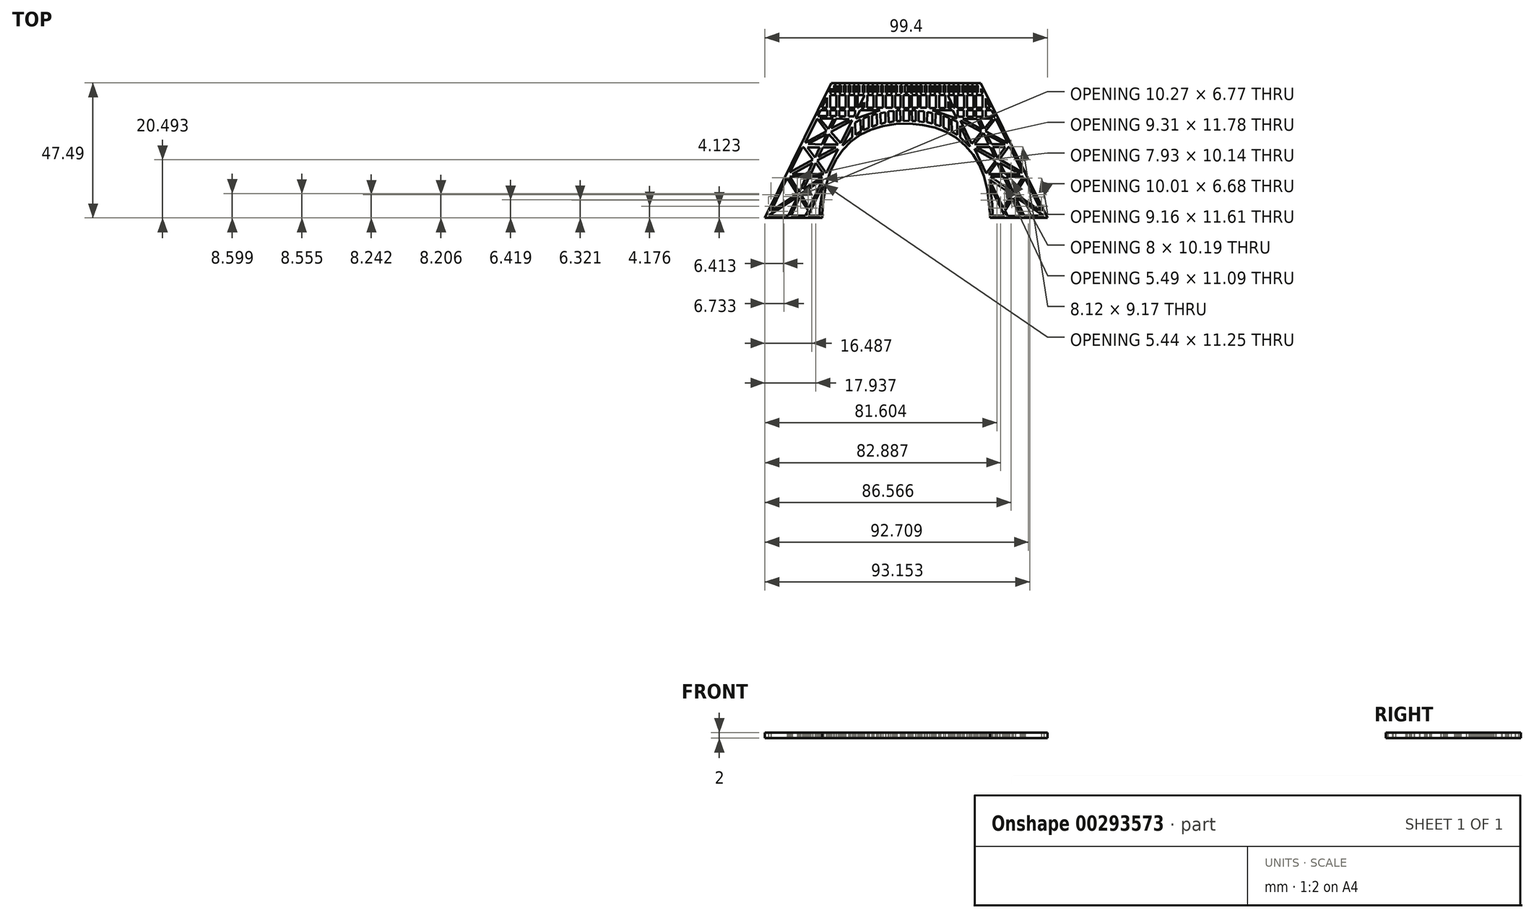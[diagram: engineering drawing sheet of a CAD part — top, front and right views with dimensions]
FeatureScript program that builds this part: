
annotation { "Feature Type Name" : "Feature", "Feature Type Description" : "" }
export const myFeature = defineFeature(function(context is Context, id is Id, definition is map)
    precondition{}
    {
        {
            var Q0;
            Q0=qCreatedBy(makeId("Top.planeOp"),FACE);
            var sketch = newSketch(context, id + "F0", { "sketchPlane" : qUnion([Q0])});
            skLineSegment(sketch, "E0", {"start": v(-25.5, 30.2) * mm, "end": v(27, 30.2) * mm});
            skLineSegment(sketch, "E1", {"start": v(27, 30.2) * mm, "end": v(50.51, -17.28) * mm});
            skLineSegment(sketch, "E2", {"start": v(50.51, -17.28) * mm, "end": v(30.37, -17.28) * mm});
            skFitSpline(sketch, "E3", {"points": [v(30.37, -17.28) * mm, v(28.52, -3.68) * mm, v(23.88, 5.66) * mm, v(16.6, 12.1) * mm, v(7.11, 15.39) * mm, v(-5.07, 15.52) * mm, v(-15.11, 12.1) * mm, v(-21.96, 6.08) * mm, v(-27.14, -4.88) * mm, v(-28.74, -16.53) * mm, v(-28.73, -17.28) * mm], "startDerivative": vector(-8.93, 118.35) * mm, "endDerivative": vector(1.13, -17.93) * mm});
            skLineSegment(sketch, "E4", {"start": v(-28.73, -17.28) * mm, "end": v(-48.89, -17.28) * mm});
            skLineSegment(sketch, "E5", {"start": v(-48.89, -17.28) * mm, "end": v(-25.5, 30.2) * mm});
            skFitSpline(sketch, "E6", {"points": [v(-28.23, -5.24) * mm, v(-29.56, -14.09) * mm, v(-29.62, -16.49) * mm], "startDerivative": vector(-2.61, -15.55) * mm, "endDerivative": vector(0.12, -5.94) * mm});
            skLineSegment(sketch, "E7", {"start": v(-29.62, -16.49) * mm, "end": v(-33.67, -16.49) * mm});
            skLineSegment(sketch, "E8", {"start": v(-33.67, -16.49) * mm, "end": v(-28.23, -5.24) * mm});
            skLineSegment(sketch, "E9", {"start": v(-33.67, -14.65) * mm, "end": v(-34.75, -16.49) * mm});
            skLineSegment(sketch, "E10", {"start": v(-34.75, -16.49) * mm, "end": v(-39.64, -16.49) * mm});
            skLineSegment(sketch, "E11", {"start": v(-39.64, -16.49) * mm, "end": v(-36.7, -10.13) * mm});
            skLineSegment(sketch, "E12", {"start": v(-36.7, -10.13) * mm, "end": v(-33.67, -14.65) * mm});
            skLineSegment(sketch, "E13", {"start": v(-47.61, -16.49) * mm, "end": v(-40.68, -16.49) * mm});
            skLineSegment(sketch, "E14", {"start": v(-40.68, -16.49) * mm, "end": v(-37.34, -9.72) * mm});
            skLineSegment(sketch, "E15", {"start": v(-37.34, -9.72) * mm, "end": v(-47.61, -16.49) * mm});
            skLineSegment(sketch, "E16", {"start": v(-41.01, -3.15) * mm, "end": v(-46.81, -14.93) * mm});
            skLineSegment(sketch, "E17", {"start": v(-46.81, -14.93) * mm, "end": v(-37.5, -8.8) * mm});
            skLineSegment(sketch, "E18", {"start": v(-37.5, -8.8) * mm, "end": v(-41.01, -3.15) * mm});
            skLineSegment(sketch, "E19", {"start": v(-33.43, -13.8) * mm, "end": v(-28.44, -3.66) * mm});
            skLineSegment(sketch, "E20", {"start": v(-28.44, -3.66) * mm, "end": v(-36.37, -8.88) * mm});
            skLineSegment(sketch, "E21", {"start": v(-36.37, -8.88) * mm, "end": v(-33.43, -13.8) * mm});
            skLineSegment(sketch, "E22", {"start": v(-40.2, -2.8) * mm, "end": v(-36.84, -8.21) * mm});
            skLineSegment(sketch, "E23", {"start": v(-36.84, -8.21) * mm, "end": v(-34.34, -2.8) * mm});
            skLineSegment(sketch, "E24", {"start": v(-34.34, -2.8) * mm, "end": v(-40.2, -2.8) * mm});
            skLineSegment(sketch, "E25", {"start": v(-35.31, -7.16) * mm, "end": v(-33.3, -2.8) * mm});
            skLineSegment(sketch, "E26", {"start": v(-33.3, -2.8) * mm, "end": v(-28.75, -2.8) * mm});
            skLineSegment(sketch, "E27", {"start": v(-28.75, -2.8) * mm, "end": v(-35.31, -7.16) * mm});
            skLineSegment(sketch, "E28", {"start": v(-39.29, -1.84) * mm, "end": v(-33.91, -1.84) * mm});
            skLineSegment(sketch, "E29", {"start": v(-33.91, -1.84) * mm, "end": v(-32.1, 2.1) * mm});
            skLineSegment(sketch, "E30", {"start": v(-32.1, 2.1) * mm, "end": v(-39.29, -1.84) * mm});
            skLineSegment(sketch, "E31", {"start": v(-31.01, 2.09) * mm, "end": v(-32.82, -1.84) * mm});
            skLineSegment(sketch, "E32", {"start": v(-32.82, -1.84) * mm, "end": v(-28.23, -1.84) * mm});
            skLineSegment(sketch, "E33", {"start": v(-28.23, -1.84) * mm, "end": v(-31.01, 2.09) * mm});
            skLineSegment(sketch, "E34", {"start": v(-30.53, 3) * mm, "end": v(-27.3, -1.46) * mm});
            skLineSegment(sketch, "E35", {"start": v(-27.3, -1.46) * mm, "end": v(-23.16, 6.95) * mm});
            skLineSegment(sketch, "E36", {"start": v(-23.16, 6.95) * mm, "end": v(-30.53, 3) * mm});
            skLineSegment(sketch, "E37", {"start": v(-40.2, -1.24) * mm, "end": v(-31.98, 3.22) * mm});
            skLineSegment(sketch, "E38", {"start": v(-31.98, 3.22) * mm, "end": v(-35.14, 7.6) * mm});
            skLineSegment(sketch, "E39", {"start": v(-35.14, 7.6) * mm, "end": v(-35.7, 7.6) * mm});
            skLineSegment(sketch, "E40", {"start": v(-35.7, 7.6) * mm, "end": v(-40.2, -1.24) * mm});
            skLineSegment(sketch, "E41", {"start": v(-33.97, 7.6) * mm, "end": v(-29.62, 7.6) * mm});
            skLineSegment(sketch, "E42", {"start": v(-29.62, 7.6) * mm, "end": v(-31.3, 3.94) * mm});
            skLineSegment(sketch, "E43", {"start": v(-31.3, 3.94) * mm, "end": v(-33.97, 7.6) * mm});
            skLineSegment(sketch, "E44", {"start": v(-28.53, 7.6) * mm, "end": v(-23.86, 7.6) * mm});
            skLineSegment(sketch, "E45", {"start": v(-23.86, 7.6) * mm, "end": v(-30.07, 4.3) * mm});
            skLineSegment(sketch, "E46", {"start": v(-30.07, 4.3) * mm, "end": v(-28.53, 7.6) * mm});
            skLineSegment(sketch, "E47", {"start": v(-29.62, 17.76) * mm, "end": v(-24.84, 17.76) * mm});
            skLineSegment(sketch, "E48", {"start": v(-24.84, 17.76) * mm, "end": v(-26.57, 14.02) * mm});
            skLineSegment(sketch, "E49", {"start": v(-26.57, 14.02) * mm, "end": v(-29.62, 17.76) * mm});
            skLineSegment(sketch, "E50", {"start": v(-23.93, 17.76) * mm, "end": v(-25.55, 14.27) * mm});
            skLineSegment(sketch, "E51", {"start": v(-25.55, 14.27) * mm, "end": v(-19.23, 17.4) * mm});
            skLineSegment(sketch, "E52", {"start": v(-19.23, 17.4) * mm, "end": v(-23.93, 17.76) * mm});
            skLineSegment(sketch, "E53", {"start": v(-30.53, 17.76) * mm, "end": v(-34.72, 9.24) * mm});
            skLineSegment(sketch, "E54", {"start": v(-34.72, 9.24) * mm, "end": v(-27.22, 13.3) * mm});
            skLineSegment(sketch, "E55", {"start": v(-27.22, 13.3) * mm, "end": v(-30.53, 17.76) * mm});
            skLineSegment(sketch, "E56", {"start": v(-18.16, 17.13) * mm, "end": v(-25.62, 12.94) * mm});
            skLineSegment(sketch, "E57", {"start": v(-25.62, 12.94) * mm, "end": v(-22.27, 9.04) * mm});
            skLineSegment(sketch, "E58", {"start": v(-22.27, 9.04) * mm, "end": v(-18.16, 17.13) * mm});
            skLineSegment(sketch, "E59", {"start": v(-33.67, 8.76) * mm, "end": v(-27.22, 12.25) * mm});
            skLineSegment(sketch, "E60", {"start": v(-27.22, 12.25) * mm, "end": v(-28.91, 8.6) * mm});
            skLineSegment(sketch, "E61", {"start": v(-28.91, 8.6) * mm, "end": v(-33.67, 8.76) * mm});
            skLineSegment(sketch, "E62", {"start": v(-28.23, 8.6) * mm, "end": v(-26.42, 12.26) * mm});
            skLineSegment(sketch, "E63", {"start": v(-26.42, 12.26) * mm, "end": v(-23.11, 8.6) * mm});
            skLineSegment(sketch, "E64", {"start": v(-23.11, 8.6) * mm, "end": v(-28.23, 8.6) * mm});
            skLineSegment(sketch, "E65", {"start": v(-30.28, 18.65) * mm, "end": v(-29.31, 20.61) * mm});
            skLineSegment(sketch, "E66", {"start": v(-29.31, 20.61) * mm, "end": v(-27, 20.61) * mm});
            skLineSegment(sketch, "E67", {"start": v(-27, 20.61) * mm, "end": v(-27, 18.52) * mm});
            skLineSegment(sketch, "E68", {"start": v(-27, 18.52) * mm, "end": v(-30.28, 18.65) * mm});
            skLineSegment(sketch, "E69", {"start": v(-25.93, 18.65) * mm, "end": v(-25.93, 20.6) * mm});
            skLineSegment(sketch, "E70", {"start": v(-25.93, 20.6) * mm, "end": v(-23.73, 20.6) * mm});
            skLineSegment(sketch, "E71", {"start": v(-23.73, 20.6) * mm, "end": v(-23.73, 18.65) * mm});
            skLineSegment(sketch, "E72", {"start": v(-23.73, 18.65) * mm, "end": v(-25.93, 18.65) * mm});
            skLineSegment(sketch, "E73", {"start": v(-22.78, 18.48) * mm, "end": v(-22.78, 20.6) * mm});
            skLineSegment(sketch, "E74", {"start": v(-22.78, 20.6) * mm, "end": v(-20.54, 20.6) * mm});
            skLineSegment(sketch, "E75", {"start": v(-20.54, 20.6) * mm, "end": v(-20.54, 18.48) * mm});
            skLineSegment(sketch, "E76", {"start": v(-20.54, 18.48) * mm, "end": v(-22.78, 18.48) * mm});
            skLineSegment(sketch, "E77", {"start": v(-19.46, 18.48) * mm, "end": v(-19.46, 20.6) * mm});
            skLineSegment(sketch, "E78", {"start": v(-19.46, 20.6) * mm, "end": v(-17.22, 20.6) * mm});
            skLineSegment(sketch, "E79", {"start": v(-17.22, 20.6) * mm, "end": v(-17.22, 19.06) * mm});
            skLineSegment(sketch, "E80", {"start": v(-17.22, 19.06) * mm, "end": v(-17.5, 18.48) * mm});
            skLineSegment(sketch, "E81", {"start": v(-17.5, 18.48) * mm, "end": v(-19.46, 18.48) * mm});
            skLineSegment(sketch, "E82", {"start": v(-14.02, 25.99) * mm, "end": v(-14.02, 25.44) * mm});
            skLineSegment(sketch, "E83", {"start": v(-14.02, 25.44) * mm, "end": v(-15.98, 21.46) * mm});
            skLineSegment(sketch, "E84", {"start": v(-15.98, 21.46) * mm, "end": v(-16.3, 21.46) * mm});
            skLineSegment(sketch, "E85", {"start": v(-16.3, 21.46) * mm, "end": v(-16.3, 25.94) * mm});
            skLineSegment(sketch, "E86", {"start": v(-16.3, 25.94) * mm, "end": v(-14.02, 25.99) * mm});
            skLineSegment(sketch, "E87", {"start": v(-14.02, 23.46) * mm, "end": v(-14.02, 21.46) * mm});
            skLineSegment(sketch, "E88", {"start": v(-14.02, 21.46) * mm, "end": v(-14.98, 21.46) * mm});
            skLineSegment(sketch, "E89", {"start": v(-14.98, 21.46) * mm, "end": v(-14.02, 23.46) * mm});
            skLineSegment(sketch, "E90", {"start": v(-19.46, 25.99) * mm, "end": v(-17.22, 25.99) * mm});
            skLineSegment(sketch, "E91", {"start": v(-17.22, 25.99) * mm, "end": v(-17.22, 21.46) * mm});
            skLineSegment(sketch, "E92", {"start": v(-17.22, 21.46) * mm, "end": v(-19.46, 21.46) * mm});
            skLineSegment(sketch, "E93", {"start": v(-19.46, 21.46) * mm, "end": v(-19.46, 25.99) * mm});
            skLineSegment(sketch, "E94", {"start": v(-22.78, 25.99) * mm, "end": v(-20.51, 25.99) * mm});
            skLineSegment(sketch, "E95", {"start": v(-20.51, 25.99) * mm, "end": v(-20.51, 21.46) * mm});
            skLineSegment(sketch, "E96", {"start": v(-20.51, 21.46) * mm, "end": v(-22.78, 21.46) * mm});
            skLineSegment(sketch, "E97", {"start": v(-22.78, 21.46) * mm, "end": v(-22.78, 25.99) * mm});
            skLineSegment(sketch, "E98", {"start": v(-25.93, 25.99) * mm, "end": v(-23.73, 25.99) * mm});
            skLineSegment(sketch, "E99", {"start": v(-23.73, 25.99) * mm, "end": v(-23.73, 21.46) * mm});
            skLineSegment(sketch, "E100", {"start": v(-23.73, 21.46) * mm, "end": v(-25.93, 21.46) * mm});
            skLineSegment(sketch, "E101", {"start": v(-25.93, 21.46) * mm, "end": v(-25.93, 25.99) * mm});
            skLineSegment(sketch, "E102", {"start": v(-27.02, 25.13) * mm, "end": v(-27.02, 21.46) * mm});
            skLineSegment(sketch, "E103", {"start": v(-27.02, 21.46) * mm, "end": v(-28.91, 21.46) * mm});
            skLineSegment(sketch, "E104", {"start": v(-28.91, 21.46) * mm, "end": v(-27.02, 25.13) * mm});
            skLineSegment(sketch, "E105", {"start": v(-25.38, 28.4) * mm, "end": v(-25.38, 26.9) * mm});
            skLineSegment(sketch, "E106", {"start": v(-25.38, 26.9) * mm, "end": v(-26.24, 26.9) * mm});
            skLineSegment(sketch, "E107", {"start": v(-26.24, 26.9) * mm, "end": v(-25.38, 28.4) * mm});
            skLineSegment(sketch, "E108", {"start": v(35.52, -14.65) * mm, "end": v(38.38, -10.18) * mm});
            skLineSegment(sketch, "E109", {"start": v(38.38, -10.18) * mm, "end": v(41.25, -16.48) * mm});
            skLineSegment(sketch, "E110", {"start": v(41.25, -16.48) * mm, "end": v(36.5, -16.57) * mm});
            skLineSegment(sketch, "E111", {"start": v(36.5, -16.57) * mm, "end": v(35.52, -14.65) * mm});
            skLineSegment(sketch, "E112", {"start": v(42.2, -16.5) * mm, "end": v(49.27, -16.5) * mm});
            skLineSegment(sketch, "E113", {"start": v(49.27, -16.5) * mm, "end": v(39.26, -9.82) * mm});
            skLineSegment(sketch, "E114", {"start": v(39.26, -9.82) * mm, "end": v(42.2, -16.5) * mm});
            skLineSegment(sketch, "E115", {"start": v(48.4, -14.88) * mm, "end": v(42.64, -3.27) * mm});
            skLineSegment(sketch, "E116", {"start": v(42.64, -3.27) * mm, "end": v(39.24, -8.66) * mm});
            skLineSegment(sketch, "E117", {"start": v(39.24, -8.66) * mm, "end": v(48.4, -14.88) * mm});
            skLineSegment(sketch, "E118", {"start": v(36.04, -2.8) * mm, "end": v(41.96, -2.8) * mm});
            skLineSegment(sketch, "E119", {"start": v(41.96, -2.8) * mm, "end": v(38.45, -8.31) * mm});
            skLineSegment(sketch, "E120", {"start": v(38.45, -8.31) * mm, "end": v(36.04, -2.8) * mm});
            skLineSegment(sketch, "E121", {"start": v(35.04, -13.78) * mm, "end": v(38, -8.93) * mm});
            skLineSegment(sketch, "E122", {"start": v(38, -8.93) * mm, "end": v(30, -3.59) * mm});
            skLineSegment(sketch, "E123", {"start": v(30, -3.59) * mm, "end": v(35.04, -13.78) * mm});
            skLineSegment(sketch, "E124", {"start": v(30.5, -2.8) * mm, "end": v(35.04, -2.8) * mm});
            skLineSegment(sketch, "E125", {"start": v(35.04, -2.8) * mm, "end": v(37.17, -7.3) * mm});
            skLineSegment(sketch, "E126", {"start": v(37.17, -7.3) * mm, "end": v(30.5, -2.8) * mm});
            skLineSegment(sketch, "E127", {"start": v(29.77, -1.8) * mm, "end": v(34.68, -1.8) * mm});
            skLineSegment(sketch, "E128", {"start": v(34.68, -1.8) * mm, "end": v(32.77, 2.26) * mm});
            skLineSegment(sketch, "E129", {"start": v(32.77, 2.26) * mm, "end": v(29.77, -1.8) * mm});
            skLineSegment(sketch, "E130", {"start": v(35.62, -1.8) * mm, "end": v(40.93, -1.8) * mm});
            skLineSegment(sketch, "E131", {"start": v(40.93, -1.8) * mm, "end": v(33.78, 2.1) * mm});
            skLineSegment(sketch, "E132", {"start": v(33.78, 2.1) * mm, "end": v(35.62, -1.8) * mm});
            skLineSegment(sketch, "E133", {"start": v(24.82, 7.07) * mm, "end": v(28.89, -1.6) * mm});
            skLineSegment(sketch, "E134", {"start": v(28.89, -1.6) * mm, "end": v(32.2, 2.9) * mm});
            skLineSegment(sketch, "E135", {"start": v(32.2, 2.9) * mm, "end": v(24.82, 7.07) * mm});
            skLineSegment(sketch, "E136", {"start": v(25.55, 7.63) * mm, "end": v(30.28, 7.63) * mm});
            skLineSegment(sketch, "E137", {"start": v(30.28, 7.63) * mm, "end": v(31.95, 4.07) * mm});
            skLineSegment(sketch, "E138", {"start": v(31.95, 4.07) * mm, "end": v(25.55, 7.63) * mm});
            skLineSegment(sketch, "E139", {"start": v(31.27, 7.63) * mm, "end": v(35.62, 7.63) * mm});
            skLineSegment(sketch, "E140", {"start": v(35.62, 7.63) * mm, "end": v(32.86, 3.88) * mm});
            skLineSegment(sketch, "E141", {"start": v(32.86, 3.88) * mm, "end": v(31.27, 7.63) * mm});
            skLineSegment(sketch, "E142", {"start": v(24.82, 8.63) * mm, "end": v(28.07, 12.59) * mm});
            skLineSegment(sketch, "E143", {"start": v(28.07, 12.59) * mm, "end": v(29.77, 8.57) * mm});
            skLineSegment(sketch, "E144", {"start": v(29.77, 8.57) * mm, "end": v(24.82, 8.63) * mm});
            skLineSegment(sketch, "E145", {"start": v(30.8, 8.63) * mm, "end": v(35.62, 8.63) * mm});
            skLineSegment(sketch, "E146", {"start": v(35.62, 8.63) * mm, "end": v(29.23, 12.02) * mm});
            skLineSegment(sketch, "E147", {"start": v(29.23, 12.02) * mm, "end": v(30.8, 8.63) * mm});
            skLineSegment(sketch, "E148", {"start": v(23.86, 8.84) * mm, "end": v(27.3, 13.01) * mm});
            skLineSegment(sketch, "E149", {"start": v(27.3, 13.01) * mm, "end": v(19.88, 16.98) * mm});
            skLineSegment(sketch, "E150", {"start": v(19.88, 16.98) * mm, "end": v(23.86, 8.84) * mm});
            skLineSegment(sketch, "E151", {"start": v(20.68, 17.58) * mm, "end": v(25.75, 17.58) * mm});
            skLineSegment(sketch, "E152", {"start": v(25.75, 17.58) * mm, "end": v(27.47, 13.93) * mm});
            skLineSegment(sketch, "E153", {"start": v(27.47, 13.93) * mm, "end": v(20.68, 17.58) * mm});
            skLineSegment(sketch, "E154", {"start": v(28.32, 14.08) * mm, "end": v(31.27, 17.66) * mm});
            skLineSegment(sketch, "E155", {"start": v(31.27, 17.66) * mm, "end": v(26.64, 17.66) * mm});
            skLineSegment(sketch, "E156", {"start": v(26.64, 17.66) * mm, "end": v(28.32, 14.08) * mm});
            skLineSegment(sketch, "E157", {"start": v(18.84, 20.74) * mm, "end": v(18.84, 18.96) * mm});
            skLineSegment(sketch, "E158", {"start": v(18.84, 18.96) * mm, "end": v(19.1, 18.39) * mm});
            skLineSegment(sketch, "E159", {"start": v(21, 20.67) * mm, "end": v(18.84, 20.74) * mm});
            skLineSegment(sketch, "E160", {"start": v(28.71, 13.26) * mm, "end": v(32.28, 17.68) * mm});
            skLineSegment(sketch, "E161", {"start": v(32.28, 17.68) * mm, "end": v(36.56, 9.04) * mm});
            skLineSegment(sketch, "E162", {"start": v(36.56, 9.04) * mm, "end": v(28.71, 13.26) * mm});
            skLineSegment(sketch, "E163", {"start": v(33.62, 3.38) * mm, "end": v(36.7, 7.55) * mm});
            skLineSegment(sketch, "E164", {"start": v(36.7, 7.55) * mm, "end": v(37.2, 7.8) * mm});
            skLineSegment(sketch, "E165", {"start": v(37.2, 7.8) * mm, "end": v(41.74, -1.37) * mm});
            skLineSegment(sketch, "E166", {"start": v(41.74, -1.37) * mm, "end": v(33.62, 3.38) * mm});
            skLineSegment(sketch, "E167", {"start": v(29.97, -5.41) * mm, "end": v(35.46, -16.5) * mm});
            skLineSegment(sketch, "E168", {"start": v(35.46, -16.5) * mm, "end": v(31.14, -16.5) * mm});
            skFitSpline(sketch, "E169", {"points": [v(29.97, -5.41) * mm, v(30.62, -8.74) * mm, v(31.1, -13.11) * mm, v(31.14, -16.5) * mm], "startDerivative": vector(2.13, -9.94) * mm, "endDerivative": vector(-0.13, -10.18) * mm});
            skLineSegment(sketch, "E170", {"start": v(19.76, 15.22) * mm, "end": v(19.76, 11.04) * mm});
            skLineSegment(sketch, "E171", {"start": v(19.76, 11.04) * mm, "end": v(23.28, 7.8) * mm});
            skLineSegment(sketch, "E172", {"start": v(23.28, 7.8) * mm, "end": v(19.76, 15.22) * mm});
            skLineSegment(sketch, "E173", {"start": v(16.76, 17.6) * mm, "end": v(18.75, 16.54) * mm});
            skLineSegment(sketch, "E174", {"start": v(18.75, 16.54) * mm, "end": v(18.75, 11.97) * mm});
            skLineSegment(sketch, "E175", {"start": v(18.75, 11.97) * mm, "end": v(16.84, 12.99) * mm});
            skLineSegment(sketch, "E176", {"start": v(16.84, 12.99) * mm, "end": v(16.76, 17.6) * mm});
            skLineSegment(sketch, "E177", {"start": v(15.87, 17.92) * mm, "end": v(15.87, 13.47) * mm});
            skLineSegment(sketch, "E178", {"start": v(15.87, 13.47) * mm, "end": v(13.98, 14.48) * mm});
            skLineSegment(sketch, "E179", {"start": v(13.98, 14.48) * mm, "end": v(13.98, 18.7) * mm});
            skLineSegment(sketch, "E180", {"start": v(13.98, 18.7) * mm, "end": v(15.87, 17.92) * mm});
            skLineSegment(sketch, "E181", {"start": v(11.17, 19.54) * mm, "end": v(12.91, 19.06) * mm});
            skLineSegment(sketch, "E182", {"start": v(12.91, 19.06) * mm, "end": v(12.91, 15) * mm});
            skLineSegment(sketch, "E183", {"start": v(12.91, 15) * mm, "end": v(11, 15.57) * mm});
            skLineSegment(sketch, "E184", {"start": v(11, 15.57) * mm, "end": v(11.17, 19.54) * mm});
            skLineSegment(sketch, "E185", {"start": v(8.17, 20.03) * mm, "end": v(9.96, 19.54) * mm});
            skLineSegment(sketch, "E186", {"start": v(9.96, 19.54) * mm, "end": v(9.96, 15.9) * mm});
            skLineSegment(sketch, "E187", {"start": v(9.96, 15.9) * mm, "end": v(8.06, 16.42) * mm});
            skLineSegment(sketch, "E188", {"start": v(8.06, 16.42) * mm, "end": v(8.17, 20.03) * mm});
            skLineSegment(sketch, "E189", {"start": v(5.14, 20.4) * mm, "end": v(7.1, 20.19) * mm});
            skLineSegment(sketch, "E190", {"start": v(7.1, 20.19) * mm, "end": v(7.1, 16.43) * mm});
            skLineSegment(sketch, "E191", {"start": v(7.1, 16.43) * mm, "end": v(5.16, 16.65) * mm});
            skLineSegment(sketch, "E192", {"start": v(5.16, 16.65) * mm, "end": v(5.14, 20.4) * mm});
            skLineSegment(sketch, "E193", {"start": v(2.83, 20.57) * mm, "end": v(4.1, 20.57) * mm});
            skLineSegment(sketch, "E194", {"start": v(4.1, 20.57) * mm, "end": v(4.1, 16.84) * mm});
            skLineSegment(sketch, "E195", {"start": v(4.1, 16.84) * mm, "end": v(2.86, 16.84) * mm});
            skLineSegment(sketch, "E196", {"start": v(2.86, 16.84) * mm, "end": v(2.83, 20.57) * mm});
            skLineSegment(sketch, "E197", {"start": v(-0.1, 20.57) * mm, "end": v(1.84, 20.59) * mm});
            skLineSegment(sketch, "E198", {"start": v(1.84, 20.59) * mm, "end": v(1.87, 16.88) * mm});
            skLineSegment(sketch, "E199", {"start": v(1.87, 16.88) * mm, "end": v(-0.16, 16.86) * mm});
            skLineSegment(sketch, "E200", {"start": v(-0.16, 16.86) * mm, "end": v(-0.1, 20.57) * mm});
            skLineSegment(sketch, "E201", {"start": v(-2.57, 20.57) * mm, "end": v(-1.24, 20.58) * mm});
            skLineSegment(sketch, "E202", {"start": v(-1.24, 20.58) * mm, "end": v(-1.22, 16.76) * mm});
            skLineSegment(sketch, "E203", {"start": v(-1.22, 16.76) * mm, "end": v(-2.57, 16.75) * mm});
            skLineSegment(sketch, "E204", {"start": v(-2.57, 16.75) * mm, "end": v(-2.57, 20.57) * mm});
            skLineSegment(sketch, "E205", {"start": v(-5.54, 20.18) * mm, "end": v(-3.63, 20.42) * mm});
            skLineSegment(sketch, "E206", {"start": v(-3.63, 20.42) * mm, "end": v(-3.63, 16.7) * mm});
            skLineSegment(sketch, "E207", {"start": v(-3.63, 16.7) * mm, "end": v(-5.38, 16.36) * mm});
            skLineSegment(sketch, "E208", {"start": v(-5.38, 16.36) * mm, "end": v(-5.54, 20.18) * mm});
            skLineSegment(sketch, "E209", {"start": v(-8.26, 19.6) * mm, "end": v(-6.5, 19.84) * mm});
            skLineSegment(sketch, "E210", {"start": v(-6.5, 19.84) * mm, "end": v(-6.5, 16.24) * mm});
            skLineSegment(sketch, "E211", {"start": v(-6.5, 16.24) * mm, "end": v(-8.2, 15.85) * mm});
            skLineSegment(sketch, "E212", {"start": v(-8.2, 15.85) * mm, "end": v(-8.26, 19.6) * mm});
            skLineSegment(sketch, "E213", {"start": v(-11.22, 18.85) * mm, "end": v(-9.5, 19.36) * mm});
            skLineSegment(sketch, "E214", {"start": v(-9.5, 19.36) * mm, "end": v(-9.44, 15.52) * mm});
            skLineSegment(sketch, "E215", {"start": v(-9.44, 15.52) * mm, "end": v(-11.22, 14.82) * mm});
            skLineSegment(sketch, "E216", {"start": v(-11.22, 14.82) * mm, "end": v(-11.22, 18.6) * mm});
            skLineSegment(sketch, "E217", {"start": v(-11.22, 18.6) * mm, "end": v(-11.22, 18.85) * mm});
            skLineSegment(sketch, "E218", {"start": v(-14.28, 17.76) * mm, "end": v(-12.4, 18.54) * mm});
            skLineSegment(sketch, "E219", {"start": v(-12.4, 18.54) * mm, "end": v(-12.34, 14.43) * mm});
            skLineSegment(sketch, "E220", {"start": v(-12.34, 14.43) * mm, "end": v(-14.2, 13.61) * mm});
            skLineSegment(sketch, "E221", {"start": v(-14.2, 13.61) * mm, "end": v(-14.28, 17.76) * mm});
            skLineSegment(sketch, "E222", {"start": v(-17.13, 16.3) * mm, "end": v(-15.22, 17.36) * mm});
            skLineSegment(sketch, "E223", {"start": v(-15.22, 17.36) * mm, "end": v(-15.13, 13.13) * mm});
            skLineSegment(sketch, "E224", {"start": v(-15.13, 13.13) * mm, "end": v(-17.04, 12) * mm});
            skLineSegment(sketch, "E225", {"start": v(-17.04, 12) * mm, "end": v(-17.13, 16.3) * mm});
            skLineSegment(sketch, "E226", {"start": v(-18.22, 14.8) * mm, "end": v(-21.58, 8.17) * mm});
            skLineSegment(sketch, "E227", {"start": v(-21.58, 8.17) * mm, "end": v(-18.22, 11.04) * mm});
            skLineSegment(sketch, "E228", {"start": v(-18.22, 11.04) * mm, "end": v(-18.22, 14.8) * mm});
            skLineSegment(sketch, "E229", {"start": v(-12.87, 25.91) * mm, "end": v(-10.64, 25.91) * mm});
            skLineSegment(sketch, "E230", {"start": v(-10.64, 25.91) * mm, "end": v(-10.64, 21.47) * mm});
            skLineSegment(sketch, "E231", {"start": v(-10.64, 21.47) * mm, "end": v(-12.94, 21.47) * mm});
            skLineSegment(sketch, "E232", {"start": v(-12.94, 21.47) * mm, "end": v(-12.87, 25.91) * mm});
            skLineSegment(sketch, "E233", {"start": v(-9.67, 25.91) * mm, "end": v(-9.67, 21.48) * mm});
            skLineSegment(sketch, "E234", {"start": v(-9.67, 21.48) * mm, "end": v(-7.4, 21.48) * mm});
            skLineSegment(sketch, "E235", {"start": v(-7.4, 21.48) * mm, "end": v(-7.4, 25.91) * mm});
            skLineSegment(sketch, "E236", {"start": v(-7.4, 25.91) * mm, "end": v(-9.67, 25.91) * mm});
            skLineSegment(sketch, "E237", {"start": v(-6.4, 25.91) * mm, "end": v(-6.4, 21.48) * mm});
            skLineSegment(sketch, "E238", {"start": v(-6.4, 21.48) * mm, "end": v(-4.14, 21.48) * mm});
            skLineSegment(sketch, "E239", {"start": v(-4.14, 21.48) * mm, "end": v(-4.14, 25.91) * mm});
            skLineSegment(sketch, "E240", {"start": v(-4.14, 25.91) * mm, "end": v(-6.4, 25.91) * mm});
            skLineSegment(sketch, "E241", {"start": v(-3.08, 25.91) * mm, "end": v(-3.08, 21.48) * mm});
            skLineSegment(sketch, "E242", {"start": v(-3.08, 21.48) * mm, "end": v(-1.14, 21.48) * mm});
            skLineSegment(sketch, "E243", {"start": v(-1.14, 21.48) * mm, "end": v(-1.14, 25.91) * mm});
            skLineSegment(sketch, "E244", {"start": v(-1.14, 25.91) * mm, "end": v(-3.08, 25.91) * mm});
            skLineSegment(sketch, "E245", {"start": v(-0.14, 25.91) * mm, "end": v(-0.14, 21.4) * mm});
            skLineSegment(sketch, "E246", {"start": v(-0.14, 21.4) * mm, "end": v(1.9, 21.4) * mm});
            skLineSegment(sketch, "E247", {"start": v(1.9, 21.4) * mm, "end": v(1.9, 25.91) * mm});
            skLineSegment(sketch, "E248", {"start": v(1.9, 25.91) * mm, "end": v(-0.14, 25.91) * mm});
            skLineSegment(sketch, "E249", {"start": v(2.82, 25.91) * mm, "end": v(2.82, 21.46) * mm});
            skLineSegment(sketch, "E250", {"start": v(2.82, 21.46) * mm, "end": v(4.9, 21.46) * mm});
            skLineSegment(sketch, "E251", {"start": v(4.9, 21.46) * mm, "end": v(4.9, 25.91) * mm});
            skLineSegment(sketch, "E252", {"start": v(4.9, 25.91) * mm, "end": v(2.82, 25.91) * mm});
            skLineSegment(sketch, "E253", {"start": v(5.83, 25.91) * mm, "end": v(5.83, 21.48) * mm});
            skLineSegment(sketch, "E254", {"start": v(5.83, 21.48) * mm, "end": v(8.04, 21.48) * mm});
            skLineSegment(sketch, "E255", {"start": v(8.04, 21.48) * mm, "end": v(8.04, 25.91) * mm});
            skLineSegment(sketch, "E256", {"start": v(8.04, 25.91) * mm, "end": v(5.83, 25.91) * mm});
            skLineSegment(sketch, "E257", {"start": v(9.01, 25.91) * mm, "end": v(9.01, 21.43) * mm});
            skLineSegment(sketch, "E258", {"start": v(9.01, 21.43) * mm, "end": v(11.3, 21.43) * mm});
            skLineSegment(sketch, "E259", {"start": v(11.3, 21.43) * mm, "end": v(11.3, 25.91) * mm});
            skLineSegment(sketch, "E260", {"start": v(11.3, 25.91) * mm, "end": v(9.01, 25.91) * mm});
            skLineSegment(sketch, "E261", {"start": v(12.39, 25.91) * mm, "end": v(12.39, 21.45) * mm});
            skLineSegment(sketch, "E262", {"start": v(12.39, 21.45) * mm, "end": v(14.63, 21.45) * mm});
            skLineSegment(sketch, "E263", {"start": v(14.63, 21.45) * mm, "end": v(14.63, 25.91) * mm});
            skLineSegment(sketch, "E264", {"start": v(14.63, 25.91) * mm, "end": v(12.39, 25.91) * mm});
            skLineSegment(sketch, "E265", {"start": v(19.1, 18.39) * mm, "end": v(21.05, 18.39) * mm});
            skLineSegment(sketch, "E266", {"start": v(21.05, 18.39) * mm, "end": v(21, 20.67) * mm});
            skLineSegment(sketch, "E267", {"start": v(22.15, 20.67) * mm, "end": v(22.15, 18.39) * mm});
            skLineSegment(sketch, "E268", {"start": v(22.15, 18.39) * mm, "end": v(24.5, 18.39) * mm});
            skLineSegment(sketch, "E269", {"start": v(24.5, 18.39) * mm, "end": v(24.5, 20.67) * mm});
            skLineSegment(sketch, "E270", {"start": v(24.5, 20.67) * mm, "end": v(22.15, 20.67) * mm});
            skLineSegment(sketch, "E271", {"start": v(25.37, 20.67) * mm, "end": v(25.37, 18.39) * mm});
            skLineSegment(sketch, "E272", {"start": v(25.37, 18.39) * mm, "end": v(27.72, 18.39) * mm});
            skLineSegment(sketch, "E273", {"start": v(27.72, 18.39) * mm, "end": v(27.72, 20.67) * mm});
            skLineSegment(sketch, "E274", {"start": v(27.72, 20.67) * mm, "end": v(25.37, 20.67) * mm});
            skLineSegment(sketch, "E275", {"start": v(28.75, 20.67) * mm, "end": v(28.75, 18.39) * mm});
            skLineSegment(sketch, "E276", {"start": v(28.75, 18.39) * mm, "end": v(32.07, 18.39) * mm});
            skLineSegment(sketch, "E277", {"start": v(32.07, 18.39) * mm, "end": v(30.84, 20.67) * mm});
            skLineSegment(sketch, "E278", {"start": v(30.84, 20.67) * mm, "end": v(28.75, 20.67) * mm});
            skLineSegment(sketch, "E279", {"start": v(28.75, 24.78) * mm, "end": v(30.39, 21.48) * mm});
            skLineSegment(sketch, "E280", {"start": v(30.39, 21.48) * mm, "end": v(28.75, 21.48) * mm});
            skLineSegment(sketch, "E281", {"start": v(28.75, 21.48) * mm, "end": v(28.75, 24.78) * mm});
            skLineSegment(sketch, "E282", {"start": v(25.37, 25.92) * mm, "end": v(27.66, 25.92) * mm});
            skLineSegment(sketch, "E283", {"start": v(27.66, 25.92) * mm, "end": v(27.66, 21.52) * mm});
            skLineSegment(sketch, "E284", {"start": v(27.66, 21.52) * mm, "end": v(25.37, 21.52) * mm});
            skLineSegment(sketch, "E285", {"start": v(25.37, 21.52) * mm, "end": v(25.37, 25.92) * mm});
            skLineSegment(sketch, "E286", {"start": v(22.15, 25.92) * mm, "end": v(24.52, 25.92) * mm});
            skLineSegment(sketch, "E287", {"start": v(24.52, 25.92) * mm, "end": v(24.52, 21.34) * mm});
            skLineSegment(sketch, "E288", {"start": v(24.52, 21.34) * mm, "end": v(22.15, 21.34) * mm});
            skLineSegment(sketch, "E289", {"start": v(22.15, 21.34) * mm, "end": v(22.15, 25.92) * mm});
            skLineSegment(sketch, "E290", {"start": v(18.8, 25.92) * mm, "end": v(21.16, 25.92) * mm});
            skLineSegment(sketch, "E291", {"start": v(21.16, 25.92) * mm, "end": v(21.16, 21.34) * mm});
            skLineSegment(sketch, "E292", {"start": v(21.16, 21.34) * mm, "end": v(18.79, 21.34) * mm});
            skLineSegment(sketch, "E293", {"start": v(18.79, 21.34) * mm, "end": v(18.8, 25.92) * mm});
            skLineSegment(sketch, "E294", {"start": v(15.54, 25.92) * mm, "end": v(17.83, 25.92) * mm});
            skLineSegment(sketch, "E295", {"start": v(17.83, 25.92) * mm, "end": v(17.83, 21.5) * mm});
            skLineSegment(sketch, "E296", {"start": v(17.83, 21.5) * mm, "end": v(17.55, 21.5) * mm});
            skLineSegment(sketch, "E297", {"start": v(17.55, 21.5) * mm, "end": v(15.55, 25.54) * mm});
            skLineSegment(sketch, "E298", {"start": v(15.55, 25.54) * mm, "end": v(15.54, 25.92) * mm});
            skLineSegment(sketch, "E299", {"start": v(-16.98, 17.66) * mm, "end": v(-15.45, 20.65) * mm});
            skLineSegment(sketch, "E300", {"start": v(-15.45, 20.65) * mm, "end": v(-8.36, 20.65) * mm});
            skLineSegment(sketch, "E301", {"start": v(-8.36, 20.65) * mm, "end": v(-16.98, 17.66) * mm});
            skLineSegment(sketch, "E302", {"start": v(10.05, 20.66) * mm, "end": v(17.1, 20.66) * mm});
            skLineSegment(sketch, "E303", {"start": v(17.1, 20.66) * mm, "end": v(18.62, 17.66) * mm});
            skLineSegment(sketch, "E304", {"start": v(18.62, 17.66) * mm, "end": v(10.05, 20.66) * mm});
            skLineSegment(sketch, "E305", {"start": v(27.16, 28.23) * mm, "end": v(27.16, 26.89) * mm});
            skLineSegment(sketch, "E306", {"start": v(27.16, 26.89) * mm, "end": v(27.9, 26.89) * mm});
            skLineSegment(sketch, "E307", {"start": v(27.9, 26.89) * mm, "end": v(27.16, 28.23) * mm});
            skLineSegment(sketch, "E308", {"start": v(25.35, 29.4) * mm, "end": v(26.03, 29.4) * mm});
            skLineSegment(sketch, "E309", {"start": v(26.03, 29.4) * mm, "end": v(26.03, 26.84) * mm});
            skLineSegment(sketch, "E310", {"start": v(26.03, 26.84) * mm, "end": v(25.33, 26.84) * mm});
            skLineSegment(sketch, "E311", {"start": v(25.33, 26.84) * mm, "end": v(25.35, 29.4) * mm});
            skLineSegment(sketch, "E312", {"start": v(23.7, 29.4) * mm, "end": v(24.44, 29.4) * mm});
            skLineSegment(sketch, "E313", {"start": v(24.44, 29.4) * mm, "end": v(24.44, 26.84) * mm});
            skLineSegment(sketch, "E314", {"start": v(24.44, 26.84) * mm, "end": v(23.76, 26.84) * mm});
            skLineSegment(sketch, "E315", {"start": v(23.76, 26.84) * mm, "end": v(23.7, 29.4) * mm});
            skLineSegment(sketch, "E316", {"start": v(22.1, 29.4) * mm, "end": v(22.82, 29.4) * mm});
            skLineSegment(sketch, "E317", {"start": v(22.82, 29.4) * mm, "end": v(22.82, 26.84) * mm});
            skLineSegment(sketch, "E318", {"start": v(22.82, 26.84) * mm, "end": v(22.14, 26.84) * mm});
            skLineSegment(sketch, "E319", {"start": v(22.14, 26.84) * mm, "end": v(22.1, 29.4) * mm});
            skLineSegment(sketch, "E320", {"start": v(15.6, 23.65) * mm, "end": v(15.6, 21.43) * mm});
            skLineSegment(sketch, "E321", {"start": v(15.6, 21.43) * mm, "end": v(16.74, 21.43) * mm});
            skLineSegment(sketch, "E322", {"start": v(16.74, 21.43) * mm, "end": v(15.6, 23.65) * mm});
            skLineSegment(sketch, "E323", {"start": v(-24.52, 29.4) * mm, "end": v(-23.77, 29.4) * mm});
            skLineSegment(sketch, "E324", {"start": v(-23.77, 29.4) * mm, "end": v(-23.77, 26.82) * mm});
            skLineSegment(sketch, "E325", {"start": v(-23.77, 26.82) * mm, "end": v(-24.47, 26.82) * mm});
            skLineSegment(sketch, "E326", {"start": v(-24.47, 26.82) * mm, "end": v(-24.52, 29.4) * mm});
            skLineSegment(sketch, "E327", {"start": v(-22.83, 29.4) * mm, "end": v(-22.83, 26.87) * mm});
            skLineSegment(sketch, "E328", {"start": v(-22.83, 26.87) * mm, "end": v(-22.1, 26.87) * mm});
            skLineSegment(sketch, "E329", {"start": v(-22.1, 26.87) * mm, "end": v(-22.1, 29.42) * mm});
            skLineSegment(sketch, "E330", {"start": v(-22.1, 29.42) * mm, "end": v(-22.83, 29.4) * mm});
            skLineSegment(sketch, "E331", {"start": v(-21.1, 29.4) * mm, "end": v(-21.1, 26.84) * mm});
            skLineSegment(sketch, "E332", {"start": v(-21.1, 26.84) * mm, "end": v(-20.51, 26.84) * mm});
            skLineSegment(sketch, "E333", {"start": v(-20.51, 26.84) * mm, "end": v(-20.51, 29.4) * mm});
            skLineSegment(sketch, "E334", {"start": v(-20.51, 29.4) * mm, "end": v(-21.1, 29.4) * mm});
            skLineSegment(sketch, "E335", {"start": v(-19.46, 29.4) * mm, "end": v(-19.46, 26.87) * mm});
            skLineSegment(sketch, "E336", {"start": v(-19.46, 26.87) * mm, "end": v(-18.78, 26.87) * mm});
            skLineSegment(sketch, "E337", {"start": v(-18.78, 26.87) * mm, "end": v(-18.78, 29.4) * mm});
            skLineSegment(sketch, "E338", {"start": v(-18.78, 29.4) * mm, "end": v(-19.46, 29.4) * mm});
            skLineSegment(sketch, "E339", {"start": v(-17.84, 29.4) * mm, "end": v(-17.84, 26.9) * mm});
            skLineSegment(sketch, "E340", {"start": v(-17.84, 26.9) * mm, "end": v(-17.16, 26.9) * mm});
            skLineSegment(sketch, "E341", {"start": v(-17.16, 26.9) * mm, "end": v(-17.16, 29.4) * mm});
            skLineSegment(sketch, "E342", {"start": v(-17.16, 29.4) * mm, "end": v(-17.84, 29.4) * mm});
            skLineSegment(sketch, "E343", {"start": v(-16.25, 29.4) * mm, "end": v(-16.25, 26.87) * mm});
            skLineSegment(sketch, "E344", {"start": v(-16.25, 26.87) * mm, "end": v(-15.6, 26.87) * mm});
            skLineSegment(sketch, "E345", {"start": v(-15.6, 26.87) * mm, "end": v(-15.6, 29.4) * mm});
            skLineSegment(sketch, "E346", {"start": v(-15.6, 29.4) * mm, "end": v(-16.25, 29.4) * mm});
            skLineSegment(sketch, "E347", {"start": v(-14.5, 29.4) * mm, "end": v(-14.5, 26.87) * mm});
            skLineSegment(sketch, "E348", {"start": v(-14.5, 26.87) * mm, "end": v(-13.93, 26.87) * mm});
            skLineSegment(sketch, "E349", {"start": v(-13.93, 26.87) * mm, "end": v(-13.93, 29.4) * mm});
            skLineSegment(sketch, "E350", {"start": v(-13.93, 29.4) * mm, "end": v(-14.5, 29.4) * mm});
            skLineSegment(sketch, "E351", {"start": v(-12.87, 29.4) * mm, "end": v(-12.87, 26.84) * mm});
            skLineSegment(sketch, "E352", {"start": v(-12.87, 26.84) * mm, "end": v(-12.2, 26.84) * mm});
            skLineSegment(sketch, "E353", {"start": v(-12.2, 26.84) * mm, "end": v(-12.2, 29.4) * mm});
            skLineSegment(sketch, "E354", {"start": v(-12.2, 29.4) * mm, "end": v(-12.87, 29.4) * mm});
            skLineSegment(sketch, "E355", {"start": v(-11.3, 29.37) * mm, "end": v(-11.3, 26.87) * mm});
            skLineSegment(sketch, "E356", {"start": v(-11.3, 26.87) * mm, "end": v(-10.58, 26.87) * mm});
            skLineSegment(sketch, "E357", {"start": v(-10.58, 26.87) * mm, "end": v(-10.58, 29.4) * mm});
            skLineSegment(sketch, "E358", {"start": v(-10.58, 29.4) * mm, "end": v(-11.3, 29.37) * mm});
            skLineSegment(sketch, "E359", {"start": v(-9.71, 29.37) * mm, "end": v(-9.71, 26.84) * mm});
            skLineSegment(sketch, "E360", {"start": v(-9.71, 26.84) * mm, "end": v(-8.98, 26.84) * mm});
            skLineSegment(sketch, "E361", {"start": v(-8.98, 26.84) * mm, "end": v(-8.98, 29.37) * mm});
            skLineSegment(sketch, "E362", {"start": v(-8.98, 29.37) * mm, "end": v(-9.71, 29.37) * mm});
            skLineSegment(sketch, "E363", {"start": v(-7.98, 29.37) * mm, "end": v(-7.98, 26.84) * mm});
            skLineSegment(sketch, "E364", {"start": v(-7.98, 26.84) * mm, "end": v(-7.32, 26.84) * mm});
            skLineSegment(sketch, "E365", {"start": v(-7.32, 26.84) * mm, "end": v(-7.32, 29.37) * mm});
            skLineSegment(sketch, "E366", {"start": v(-7.32, 29.37) * mm, "end": v(-7.98, 29.37) * mm});
            skLineSegment(sketch, "E367", {"start": v(-6.34, 29.37) * mm, "end": v(-6.34, 26.87) * mm});
            skLineSegment(sketch, "E368", {"start": v(-6.34, 26.87) * mm, "end": v(-5.59, 26.87) * mm});
            skLineSegment(sketch, "E369", {"start": v(-5.59, 26.87) * mm, "end": v(-5.59, 29.37) * mm});
            skLineSegment(sketch, "E370", {"start": v(-5.59, 29.37) * mm, "end": v(-6.34, 29.37) * mm});
            skLineSegment(sketch, "E371", {"start": v(-4.7, 29.35) * mm, "end": v(-4.7, 26.89) * mm});
            skLineSegment(sketch, "E372", {"start": v(-4.7, 26.89) * mm, "end": v(-4, 26.89) * mm});
            skLineSegment(sketch, "E373", {"start": v(-4, 26.89) * mm, "end": v(-4, 29.38) * mm});
            skLineSegment(sketch, "E374", {"start": v(-4, 29.38) * mm, "end": v(-4.7, 29.35) * mm});
            skLineSegment(sketch, "E375", {"start": v(-3.09, 29.35) * mm, "end": v(-3.09, 26.86) * mm});
            skLineSegment(sketch, "E376", {"start": v(-3.09, 26.86) * mm, "end": v(-2.39, 26.86) * mm});
            skLineSegment(sketch, "E377", {"start": v(-2.39, 26.86) * mm, "end": v(-2.39, 29.35) * mm});
            skLineSegment(sketch, "E378", {"start": v(-2.39, 29.35) * mm, "end": v(-3.09, 29.35) * mm});
            skLineSegment(sketch, "E379", {"start": v(-1.35, 29.35) * mm, "end": v(-1.35, 26.86) * mm});
            skLineSegment(sketch, "E380", {"start": v(-1.35, 26.86) * mm, "end": v(-0.72, 26.86) * mm});
            skLineSegment(sketch, "E381", {"start": v(-0.72, 26.86) * mm, "end": v(-0.72, 29.32) * mm});
            skLineSegment(sketch, "E382", {"start": v(-0.72, 29.32) * mm, "end": v(-1.35, 29.35) * mm});
            skLineSegment(sketch, "E383", {"start": v(0.38, 29.35) * mm, "end": v(0.38, 26.86) * mm});
            skLineSegment(sketch, "E384", {"start": v(0.38, 26.86) * mm, "end": v(1.32, 26.86) * mm});
            skLineSegment(sketch, "E385", {"start": v(1.32, 26.86) * mm, "end": v(1.32, 29.35) * mm});
            skLineSegment(sketch, "E386", {"start": v(1.32, 29.35) * mm, "end": v(0.38, 29.35) * mm});
            skLineSegment(sketch, "E387", {"start": v(2.3, 29.38) * mm, "end": v(2.3, 26.86) * mm});
            skLineSegment(sketch, "E388", {"start": v(2.3, 26.86) * mm, "end": v(3.14, 26.86) * mm});
            skLineSegment(sketch, "E389", {"start": v(3.14, 26.86) * mm, "end": v(3.14, 29.35) * mm});
            skLineSegment(sketch, "E390", {"start": v(3.14, 29.35) * mm, "end": v(2.3, 29.38) * mm});
            skLineSegment(sketch, "E391", {"start": v(4.02, 29.35) * mm, "end": v(4.02, 26.86) * mm});
            skLineSegment(sketch, "E392", {"start": v(4.02, 26.86) * mm, "end": v(4.75, 26.86) * mm});
            skLineSegment(sketch, "E393", {"start": v(4.75, 26.86) * mm, "end": v(4.75, 29.38) * mm});
            skLineSegment(sketch, "E394", {"start": v(4.75, 29.38) * mm, "end": v(4.02, 29.35) * mm});
            skLineSegment(sketch, "E395", {"start": v(5.6, 29.35) * mm, "end": v(5.6, 26.86) * mm});
            skLineSegment(sketch, "E396", {"start": v(5.6, 26.86) * mm, "end": v(6.36, 26.86) * mm});
            skLineSegment(sketch, "E397", {"start": v(6.36, 26.86) * mm, "end": v(6.36, 29.35) * mm});
            skLineSegment(sketch, "E398", {"start": v(6.36, 29.35) * mm, "end": v(5.6, 29.35) * mm});
            skLineSegment(sketch, "E399", {"start": v(7.35, 29.35) * mm, "end": v(7.35, 26.86) * mm});
            skLineSegment(sketch, "E400", {"start": v(7.35, 26.86) * mm, "end": v(7.93, 26.86) * mm});
            skLineSegment(sketch, "E401", {"start": v(7.93, 26.86) * mm, "end": v(7.93, 29.35) * mm});
            skLineSegment(sketch, "E402", {"start": v(7.93, 29.35) * mm, "end": v(7.35, 29.35) * mm});
            skLineSegment(sketch, "E403", {"start": v(8.96, 29.35) * mm, "end": v(8.96, 26.86) * mm});
            skLineSegment(sketch, "E404", {"start": v(8.96, 26.86) * mm, "end": v(9.69, 26.86) * mm});
            skLineSegment(sketch, "E405", {"start": v(9.69, 26.86) * mm, "end": v(9.69, 29.38) * mm});
            skLineSegment(sketch, "E406", {"start": v(9.69, 29.38) * mm, "end": v(8.96, 29.35) * mm});
            skLineSegment(sketch, "E407", {"start": v(10.57, 29.35) * mm, "end": v(10.57, 26.86) * mm});
            skLineSegment(sketch, "E408", {"start": v(10.57, 26.86) * mm, "end": v(11.3, 26.86) * mm});
            skLineSegment(sketch, "E409", {"start": v(11.3, 26.86) * mm, "end": v(11.3, 29.38) * mm});
            skLineSegment(sketch, "E410", {"start": v(11.3, 29.38) * mm, "end": v(10.57, 29.35) * mm});
            skLineSegment(sketch, "E411", {"start": v(12.18, 29.42) * mm, "end": v(12.18, 26.86) * mm});
            skLineSegment(sketch, "E412", {"start": v(12.18, 26.86) * mm, "end": v(12.91, 26.86) * mm});
            skLineSegment(sketch, "E413", {"start": v(12.91, 26.86) * mm, "end": v(12.91, 29.38) * mm});
            skLineSegment(sketch, "E414", {"start": v(12.91, 29.38) * mm, "end": v(12.18, 29.42) * mm});
            skLineSegment(sketch, "E415", {"start": v(13.94, 29.35) * mm, "end": v(13.94, 26.86) * mm});
            skLineSegment(sketch, "E416", {"start": v(13.94, 26.86) * mm, "end": v(14.55, 26.86) * mm});
            skLineSegment(sketch, "E417", {"start": v(14.55, 26.86) * mm, "end": v(14.55, 29.42) * mm});
            skLineSegment(sketch, "E418", {"start": v(14.55, 29.42) * mm, "end": v(13.94, 29.35) * mm});
            skLineSegment(sketch, "E419", {"start": v(14.55, 29.42) * mm, "end": v(13.94, 29.42) * mm});
            skLineSegment(sketch, "E420", {"start": v(13.94, 29.42) * mm, "end": v(13.94, 29.35) * mm});
            skLineSegment(sketch, "E421", {"start": v(12.18, 29.42) * mm, "end": v(12.9, 29.42) * mm});
            skLineSegment(sketch, "E422", {"start": v(12.9, 29.42) * mm, "end": v(12.91, 29.35) * mm});
            skLineSegment(sketch, "E423", {"start": v(15.54, 29.42) * mm, "end": v(15.54, 26.84) * mm});
            skLineSegment(sketch, "E424", {"start": v(15.54, 26.84) * mm, "end": v(16.3, 26.84) * mm});
            skLineSegment(sketch, "E425", {"start": v(16.3, 26.84) * mm, "end": v(16.3, 29.42) * mm});
            skLineSegment(sketch, "E426", {"start": v(16.3, 29.42) * mm, "end": v(15.54, 29.42) * mm});
            skLineSegment(sketch, "E427", {"start": v(17.14, 29.38) * mm, "end": v(17.14, 26.86) * mm});
            skLineSegment(sketch, "E428", {"start": v(17.14, 26.86) * mm, "end": v(17.86, 26.86) * mm});
            skLineSegment(sketch, "E429", {"start": v(17.86, 26.86) * mm, "end": v(17.86, 29.42) * mm});
            skLineSegment(sketch, "E430", {"start": v(17.86, 29.42) * mm, "end": v(17.14, 29.38) * mm});
            skLineSegment(sketch, "E431", {"start": v(18.75, 29.38) * mm, "end": v(18.75, 26.84) * mm});
            skLineSegment(sketch, "E432", {"start": v(18.75, 26.84) * mm, "end": v(19.53, 26.84) * mm});
            skLineSegment(sketch, "E433", {"start": v(19.53, 26.84) * mm, "end": v(19.53, 29.42) * mm});
            skLineSegment(sketch, "E434", {"start": v(19.53, 29.42) * mm, "end": v(18.75, 29.38) * mm});
            skLineSegment(sketch, "E435", {"start": v(20.49, 29.38) * mm, "end": v(20.49, 26.8) * mm});
            skLineSegment(sketch, "E436", {"start": v(20.49, 26.8) * mm, "end": v(21.12, 26.8) * mm});
            skLineSegment(sketch, "E437", {"start": v(21.12, 26.8) * mm, "end": v(21.12, 29.38) * mm});
            skLineSegment(sketch, "E438", {"start": v(21.12, 29.38) * mm, "end": v(20.49, 29.38) * mm});
            skLineSegment(sketch, "E439", {"start": v(19.53, 29.42) * mm, "end": v(18.75, 29.42) * mm});
            skLineSegment(sketch, "E440", {"start": v(18.75, 29.42) * mm, "end": v(18.75, 29.38) * mm});
            skLineSegment(sketch, "E441", {"start": v(17.86, 29.42) * mm, "end": v(17.13, 29.42) * mm});
            skLineSegment(sketch, "E442", {"start": v(17.13, 29.42) * mm, "end": v(17.14, 29.38) * mm});
            skSolve(sketch);
        }
        {
            var Q0;
            Q0=makeQuery(id+"F0.imprint","IMPRINT",FACE,{"disambiguationData":[TD([[makeQuery(id+"F0.imprint","IMPRINT",EDGE,{"derivedFrom":sQuery(id+"F0.wireOp",EDGE,"E0")}),-1.0]])]});
            extrude(context, id + "F1", {"entities" : qUnion([Q0]), "depth" : 2 * mm, "offsetDistance" : 25 * mm});
        }
    });
